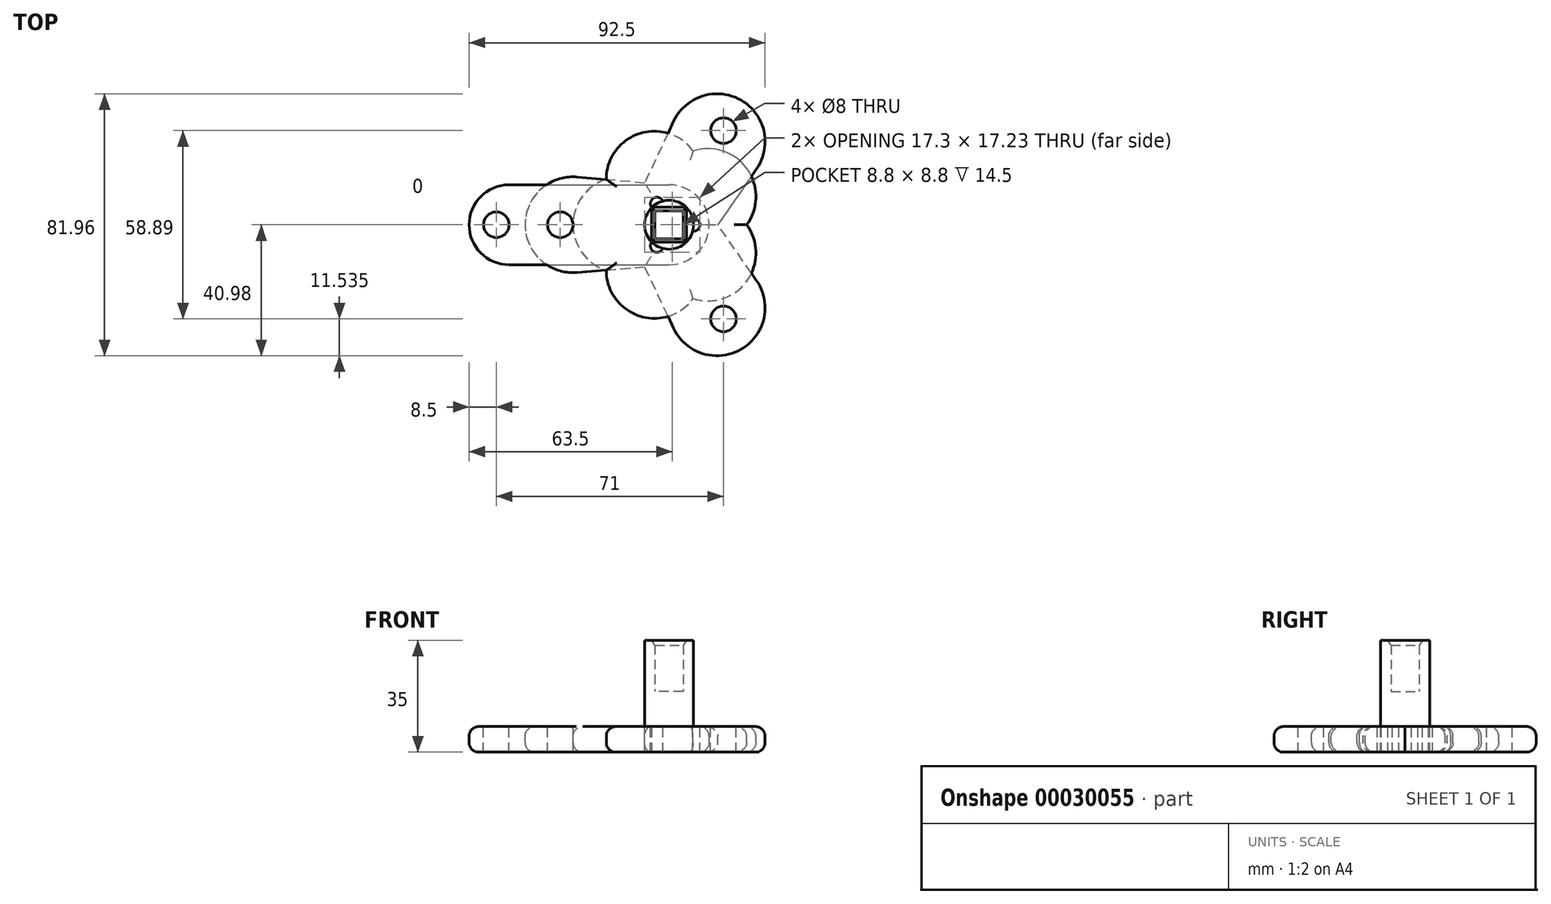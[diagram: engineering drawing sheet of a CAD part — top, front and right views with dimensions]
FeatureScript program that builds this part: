
annotation { "Feature Type Name" : "Feature", "Feature Type Description" : "" }
export const myFeature = defineFeature(function(context is Context, id is Id, definition is map)
    precondition{}
    {
        {
            var Q0;
            Q0=qCreatedBy(makeId("Top.planeOp"),FACE);
            var sketch = newSketch(context, id + "F0", { "sketchPlane" : qUnion([Q0])});
            skLineSegment(sketch, "E0.rect.bottom", {"start": v(4.4, -4.4) * mm, "end": v(-4.4, -4.4) * mm});
            skLineSegment(sketch, "E0.rect.top", {"start": v(4.4, 4.4) * mm, "end": v(-4.4, 4.4) * mm});
            skLineSegment(sketch, "E0.rect.left", {"start": v(4.4, -4.4) * mm, "end": v(4.4, 4.4) * mm});
            skLineSegment(sketch, "E0.rect.right", {"start": v(-4.4, -4.4) * mm, "end": v(-4.4, 4.4) * mm});
            skPoint(sketch, "E0.rect.middle", {"position": v(0, 0) * mm});
            skCircle(sketch, "E1", {"center": v(0, 0) * mm, "radius": 7.65 * mm});
            skArc(sketch, "E2", {"start": v(7.39, -1.98) * mm, "mid": v(9.65, 0) * mm, "end": v(7.39, 1.98) * mm});
            skArc(sketch, "E3.1.0", {"start": v(-1.98, 7.4) * mm, "mid": v(-4.82, 8.36) * mm, "end": v(-5.41, 5.4) * mm});
            skArc(sketch, "E3.2.0", {"start": v(-5.41, -5.4) * mm, "mid": v(-4.82, -8.36) * mm, "end": v(-1.98, -7.4) * mm});
            skSolve(sketch);
        }
        {
            var Q0;
            Q0=makeQuery(id+"F0.imprint","IMPRINT",FACE,{"disambiguationData":[TD([[makeQuery(id+"F0.imprint","IMPRINT",EDGE,{"derivedFrom":sQuery(id+"F0.wireOp",EDGE,"E0.rect.bottom")}),1.0]])]});
            extrude(context, id + "F1", {"entities" : qUnion([Q0]), "depth" : 27 * mm});
        }
        {
            var Q0;
            Q0=makeQuery(id+"F0.imprint","IMPRINT",FACE,{"disambiguationData":[TD([[makeQuery(id+"F0.imprint","IMPRINT",EDGE,{"derivedFrom":sQuery(id+"F0.wireOp",EDGE,"E0.rect.bottom")}),-1.0]])]});
            extrude(context, id + "F2", {"entities" : qUnion([Q0]), "operationType" : NewBodyOperationType.ADD, "depth" : 11 * mm});
        }
        {
            var Q0;
            Q0=makeQuery(id+"F1.opExtrude","CAP_EDGE",EDGE,{"disambiguationData":[OSD([sQuery(id+"F0.wireOp",EDGE,"E0.rect.top")])],"isStart":false});
            var Q1;
            Q1=makeQuery(id+"F1.opExtrude","CAP_EDGE",EDGE,{"disambiguationData":[OSD([sQuery(id+"F0.wireOp",EDGE,"E0.rect.right")])],"isStart":false});
            var Q2;
            Q2=makeQuery(id+"F1.opExtrude","CAP_EDGE",EDGE,{"disambiguationData":[OSD([sQuery(id+"F0.wireOp",EDGE,"E0.rect.bottom")])],"isStart":false});
            var Q3;
            Q3=makeQuery(id+"F1.opExtrude","CAP_EDGE",EDGE,{"disambiguationData":[OSD([sQuery(id+"F0.wireOp",EDGE,"E0.rect.left")])],"isStart":false});
            chamfer(context, id + "F3", {"entities" : qUnion([Q0, Q1, Q2, Q3]), "chamferType" : ChamferType.OFFSET_ANGLE, "width" : 1.5 * mm, "oppositeDirection" : false, "angle" : 35 * degree, "tangentPropagation" : true});
        }
        {
            var Q0;
            {var subQ0=sQuery(id+"F0.wireOp",EDGE,"E3.1.0");Q0=makeQuery(id+"F0.imprint","IMPRINT",FACE,{"disambiguationData":[TD([[makeQuery(id+"F0.imprint","IMPRINT",EDGE,{"derivedFrom":subQ0}),1.0]])]});}
            var Q1;
            {var subQ0=sQuery(id+"F0.wireOp",EDGE,"E3.2.0");Q1=makeQuery(id+"F0.imprint","IMPRINT",FACE,{"disambiguationData":[TD([[makeQuery(id+"F0.imprint","IMPRINT",EDGE,{"derivedFrom":subQ0}),1.0]])]});}
            var Q2;
            {var subQ0=sQuery(id+"F0.wireOp",EDGE,"E2");Q2=makeQuery(id+"F0.imprint","IMPRINT",FACE,{"disambiguationData":[TD([[makeQuery(id+"F0.imprint","IMPRINT",EDGE,{"derivedFrom":subQ0}),1.0]])]});}
            var Q3;
            Q3=makeQuery(id+"F0.imprint","IMPRINT",FACE,{"disambiguationData":[TD([[makeQuery(id+"F0.imprint","IMPRINT",EDGE,{"derivedFrom":sQuery(id+"F0.wireOp",EDGE,"E0.rect.bottom")}),1.0]])]});
            var Q4;
            Q4=makeQuery(id+"F0.imprint","IMPRINT",FACE,{"disambiguationData":[TD([[makeQuery(id+"F0.imprint","IMPRINT",EDGE,{"derivedFrom":sQuery(id+"F0.wireOp",EDGE,"E0.rect.bottom")}),-1.0]])]});
            extrude(context, id + "F4", {"entities" : qUnion([Q0, Q1, Q2, Q3, Q4]), "oppositeDirection" : true, "depth" : 8 * mm});
        }
        {
            var Q0;
            Q0=qCreatedBy(makeId("Top.planeOp"),FACE);
            var sketch = newSketch(context, id + "F5", { "sketchPlane" : qUnion([Q0])});
            skPoint(sketch, "E4.rect.middle", {"position": v(0, 0) * mm});
            skCircle(sketch, "E5", {"center": v(0, 0) * mm, "radius": 12.5 * mm});
            skCircle(sketch, "E6", {"center": v(-50, 0) * mm, "radius": 12.5 * mm});
            skLineSegment(sketch, "E7", {"start": v(-50, 12.5) * mm, "end": v(0, 12.5) * mm});
            skLineSegment(sketch, "E8", {"start": v(-50, -12.5) * mm, "end": v(0, -12.5) * mm});
            skLineSegment(sketch, "E9", {"start": v(-50, 0) * mm, "end": v(0, 0) * mm, "construction": true});
            skCircle(sketch, "E10", {"center": v(-54, 0) * mm, "radius": 4 * mm});
            skSolve(sketch);
        }
        {
            var Q0;
            Q0=makeQuery(id+"F5.imprint","IMPRINT",FACE,{"disambiguationData":[TD([[makeQuery(id+"F5.imprint","IMPRINT",EDGE,{"derivedFrom":sQuery(id+"F5.wireOp",EDGE,"E10")}),-1.0]])]});
            var Q1;
            {var subQ1=sQuery(id+"F5.wireOp",EDGE,"E7");Q1=makeQuery(id+"F5.imprint","IMPRINT",FACE,{"disambiguationData":[TD([[makeQuery(id+"F5.imprint","IMPRINT",EDGE,{"derivedFrom":subQ1}),-1.0]])]});}
            var Q2;
            {var subQ0=sQuery(id+"F5.wireOp",EDGE,"E5");var subQ2=makeQuery(id+"F5.imprint","INTERSECT",VERTEX,{"derivedFrom":[subQ0,sQuery(id+"F5.wireOp",EDGE,"E7")]});Q2=makeQuery(id+"F5.imprint","IMPRINT",FACE,{"disambiguationData":[TD([[makeQuery(id+"F5.imprint","IMPRINT",EDGE,{"disambiguationData":[TD([[subQ2,-1.0]])],"derivedFrom":subQ0}),1.0]])]});}
            extrude(context, id + "F6", {"entities" : qUnion([Q0, Q1, Q2]), "oppositeDirection" : true, "depth" : 8 * mm});
        }
        {
            var Q0;
            Q0=makeQuery(id+"F0.imprint","IMPRINT",FACE,{"disambiguationData":[TD([[makeQuery(id+"F0.imprint","IMPRINT",EDGE,{"derivedFrom":sQuery(id+"F0.wireOp",EDGE,"E0.rect.bottom")}),1.0]])]});
            var Q1;
            Q1=makeQuery(id+"F0.imprint","IMPRINT",FACE,{"disambiguationData":[TD([[makeQuery(id+"F0.imprint","IMPRINT",EDGE,{"derivedFrom":sQuery(id+"F0.wireOp",EDGE,"E0.rect.bottom")}),-1.0]])]});
            var Q2;
            {var subQ0=sQuery(id+"F0.wireOp",EDGE,"E3.2.0");Q2=makeQuery(id+"F0.imprint","IMPRINT",FACE,{"disambiguationData":[TD([[makeQuery(id+"F0.imprint","IMPRINT",EDGE,{"derivedFrom":subQ0}),1.0]])]});}
            var Q3;
            {var subQ0=sQuery(id+"F0.wireOp",EDGE,"E2");Q3=makeQuery(id+"F0.imprint","IMPRINT",FACE,{"disambiguationData":[TD([[makeQuery(id+"F0.imprint","IMPRINT",EDGE,{"derivedFrom":subQ0}),1.0]])]});}
            var Q4;
            {var subQ0=sQuery(id+"F0.wireOp",EDGE,"E3.1.0");Q4=makeQuery(id+"F0.imprint","IMPRINT",FACE,{"disambiguationData":[TD([[makeQuery(id+"F0.imprint","IMPRINT",EDGE,{"derivedFrom":subQ0}),1.0]])]});}
            var Q5;
            Q5=makeQuery(id+"F6.opExtrude","SWEPT_BODY",BODY,{"disambiguationData":[OSD([sQuery(id+"F5.wireOp",EDGE,"E5"),sQuery(id+"F5.wireOp",EDGE,"E6"),sQuery(id+"F5.wireOp",EDGE,"E7"),sQuery(id+"F5.wireOp",EDGE,"E8"),sQuery(id+"F5.wireOp",EDGE,"E10")])]});
            extrude(context, id + "F7", {"entities" : qUnion([Q0, Q1, Q2, Q3, Q4]), "operationType" : NewBodyOperationType.REMOVE, "endBound" : BoundingType.UP_TO_BODY, "oppositeDirection" : true, "endBoundEntityBody" : qUnion([Q5]), "depth" : 5 * mm});
        }
        {
            var Q0;
            Q0=makeQuery(id+"F6.opExtrude","CAP_EDGE",EDGE,{"disambiguationData":[OSD([sQuery(id+"F5.wireOp",EDGE,"E8")])],"isStart":true});
            var Q1;
            Q1=makeQuery(id+"F6.opExtrude","CAP_EDGE",EDGE,{"disambiguationData":[OSD([sQuery(id+"F5.wireOp",EDGE,"E8")])],"isStart":false});
            fillet(context, id + "F8", {"entities" : qUnion([Q0, Q1]), "radius" : 3 * mm, "tangentPropagation" : true, "allowEdgeOverflow" : false});
        }
        {
            var Q0;
            Q0=qCreatedBy(makeId("Top.planeOp"),FACE);
            var sketch = newSketch(context, id + "F9", { "sketchPlane" : qUnion([Q0])});
            skCircle(sketch, "E11", {"center": v(0, 0) * mm, "radius": 15 * mm});
            skCircle(sketch, "E12", {"center": v(-15, 0) * mm, "radius": 15 * mm});
            skCircle(sketch, "E13.1.0", {"center": v(-4.64, -14.27) * mm, "radius": 15 * mm});
            skCircle(sketch, "E13.2.0", {"center": v(12.14, -8.82) * mm, "radius": 15 * mm});
            skCircle(sketch, "E14.1.3.0", {"center": v(12.14, 8.82) * mm, "radius": 15 * mm});
            skCircle(sketch, "E14.1.4.0", {"center": v(-4.64, 14.27) * mm, "radius": 15 * mm});
            skSolve(sketch);
        }
        {
            var Q0;
            {var subQ0=sQuery(id+"F9.wireOp",EDGE,"E14.1.4.0");var subQ1=sQuery(id+"F9.wireOp",EDGE,"E11");var subQ2=makeQuery(id+"F9.imprint","INTERSECT",VERTEX,{"disambiguationData":[OD(0.0)],"derivedFrom":[subQ1,subQ0]});Q0=makeQuery(id+"F9.imprint","IMPRINT",FACE,{"disambiguationData":[TD([[makeQuery(id+"F9.imprint","IMPRINT",EDGE,{"disambiguationData":[TD([[subQ2,1.0]])],"derivedFrom":subQ1}),-1.0]])]});}
            var Q1;
            {var subQ1=sQuery(id+"F9.wireOp",EDGE,"E14.1.3.0");var subQ5=sQuery(id+"F9.wireOp",EDGE,"E11");var subQ6=makeQuery(id+"F9.imprint","INTERSECT",VERTEX,{"disambiguationData":[OD(0.0)],"derivedFrom":[subQ5,subQ1]});Q1=makeQuery(id+"F9.imprint","IMPRINT",FACE,{"disambiguationData":[TD([[makeQuery(id+"F9.imprint","IMPRINT",EDGE,{"disambiguationData":[TD([[subQ6,-1.0]])],"derivedFrom":subQ5}),-1.0]])]});}
            var Q2;
            {var subQ1=sQuery(id+"F9.wireOp",EDGE,"E11");var subQ3=sQuery(id+"F9.wireOp",EDGE,"E12");var subQ5=makeQuery(id+"F9.imprint","INTERSECT",VERTEX,{"disambiguationData":[OD(0.0)],"derivedFrom":[subQ1,subQ3]});Q2=makeQuery(id+"F9.imprint","IMPRINT",FACE,{"disambiguationData":[TD([[makeQuery(id+"F9.imprint","IMPRINT",EDGE,{"disambiguationData":[TD([[subQ5,-1.0]])],"derivedFrom":subQ1}),-1.0]])]});}
            var Q3;
            {var subQ0=sQuery(id+"F9.wireOp",EDGE,"E14.1.4.0");var subQ1=sQuery(id+"F9.wireOp",EDGE,"E11");var subQ2=makeQuery(id+"F9.imprint","INTERSECT",VERTEX,{"disambiguationData":[OD(1.0)],"derivedFrom":[subQ1,subQ0]});Q3=makeQuery(id+"F9.imprint","IMPRINT",FACE,{"disambiguationData":[TD([[makeQuery(id+"F9.imprint","IMPRINT",EDGE,{"disambiguationData":[TD([[subQ2,-1.0]])],"derivedFrom":subQ1}),-1.0]])]});}
            var Q4;
            {var subQ1=sQuery(id+"F9.wireOp",EDGE,"E11");var subQ5=sQuery(id+"F9.wireOp",EDGE,"E12");var subQ7=makeQuery(id+"F9.imprint","INTERSECT",VERTEX,{"disambiguationData":[OD(1.0)],"derivedFrom":[subQ1,subQ5]});Q4=makeQuery(id+"F9.imprint","IMPRINT",FACE,{"disambiguationData":[TD([[makeQuery(id+"F9.imprint","IMPRINT",EDGE,{"disambiguationData":[TD([[subQ7,-1.0]])],"derivedFrom":subQ1}),-1.0]])]});}
            var Q5;
            {var subQ0=sQuery(id+"F9.wireOp",EDGE,"E13.2.0");var subQ1=sQuery(id+"F9.wireOp",EDGE,"E11");var subQ2=makeQuery(id+"F9.imprint","INTERSECT",VERTEX,{"disambiguationData":[OD(1.0)],"derivedFrom":[subQ1,subQ0]});Q5=makeQuery(id+"F9.imprint","IMPRINT",FACE,{"disambiguationData":[TD([[makeQuery(id+"F9.imprint","IMPRINT",EDGE,{"disambiguationData":[TD([[subQ2,-1.0]])],"derivedFrom":subQ1}),-1.0]])]});}
            var Q6;
            {var subQ1=sQuery(id+"F9.wireOp",EDGE,"E11");var subQ5=sQuery(id+"F9.wireOp",EDGE,"E13.1.0");var subQ7=makeQuery(id+"F9.imprint","INTERSECT",VERTEX,{"disambiguationData":[OD(1.0)],"derivedFrom":[subQ1,subQ5]});Q6=makeQuery(id+"F9.imprint","IMPRINT",FACE,{"disambiguationData":[TD([[makeQuery(id+"F9.imprint","IMPRINT",EDGE,{"disambiguationData":[TD([[subQ7,-1.0]])],"derivedFrom":subQ1}),-1.0]])]});}
            var Q7;
            {var subQ1=sQuery(id+"F9.wireOp",EDGE,"E11");var subQ3=sQuery(id+"F9.wireOp",EDGE,"E13.2.0");var subQ5=makeQuery(id+"F9.imprint","INTERSECT",VERTEX,{"disambiguationData":[OD(0.0)],"derivedFrom":[subQ1,subQ3]});Q7=makeQuery(id+"F9.imprint","IMPRINT",FACE,{"disambiguationData":[TD([[makeQuery(id+"F9.imprint","IMPRINT",EDGE,{"disambiguationData":[TD([[subQ5,1.0]])],"derivedFrom":subQ1}),-1.0]])]});}
            var Q8;
            {var subQ0=sQuery(id+"F9.wireOp",EDGE,"E14.1.4.0");var subQ3=sQuery(id+"F9.wireOp",EDGE,"E11");var subQ4=makeQuery(id+"F9.imprint","INTERSECT",VERTEX,{"disambiguationData":[OD(0.0)],"derivedFrom":[subQ3,subQ0]});Q8=makeQuery(id+"F9.imprint","IMPRINT",FACE,{"disambiguationData":[TD([[makeQuery(id+"F9.imprint","IMPRINT",EDGE,{"disambiguationData":[TD([[subQ4,-1.0]])],"derivedFrom":subQ3}),1.0]])]});}
            var Q9;
            {var subQ0=sQuery(id+"F9.wireOp",EDGE,"E13.2.0");var subQ1=sQuery(id+"F9.wireOp",EDGE,"E12");var subQ3=makeQuery(id+"F9.imprint","INTERSECT",VERTEX,{"derivedFrom":[subQ1,subQ0]});Q9=makeQuery(id+"F9.imprint","IMPRINT",FACE,{"disambiguationData":[TD([[makeQuery(id+"F9.imprint","IMPRINT",EDGE,{"disambiguationData":[TD([[subQ3,-1.0]])],"derivedFrom":subQ1}),1.0]])]});}
            var Q10;
            {var subQ1=sQuery(id+"F9.wireOp",EDGE,"E13.1.0");var subQ3=sQuery(id+"F9.wireOp",EDGE,"E11");var subQ5=makeQuery(id+"F9.imprint","INTERSECT",VERTEX,{"disambiguationData":[OD(1.0)],"derivedFrom":[subQ3,subQ1]});Q10=makeQuery(id+"F9.imprint","IMPRINT",FACE,{"disambiguationData":[TD([[makeQuery(id+"F9.imprint","IMPRINT",EDGE,{"disambiguationData":[TD([[subQ5,-1.0]])],"derivedFrom":subQ3}),1.0]])]});}
            var Q11;
            {var subQ3=sQuery(id+"F9.wireOp",EDGE,"E11");var subQ6=sQuery(id+"F9.wireOp",EDGE,"E12");var subQ9=makeQuery(id+"F9.imprint","INTERSECT",VERTEX,{"disambiguationData":[OD(0.0)],"derivedFrom":[subQ3,subQ6]});Q11=makeQuery(id+"F9.imprint","IMPRINT",FACE,{"disambiguationData":[TD([[makeQuery(id+"F9.imprint","IMPRINT",EDGE,{"disambiguationData":[TD([[subQ9,-1.0]])],"derivedFrom":subQ3}),1.0]])]});}
            var Q12;
            {var subQ0=sQuery(id+"F9.wireOp",EDGE,"E14.1.4.0");var subQ1=sQuery(id+"F9.wireOp",EDGE,"E13.1.0");var subQ3=makeQuery(id+"F9.imprint","INTERSECT",VERTEX,{"derivedFrom":[subQ1,subQ0]});Q12=makeQuery(id+"F9.imprint","IMPRINT",FACE,{"disambiguationData":[TD([[makeQuery(id+"F9.imprint","IMPRINT",EDGE,{"disambiguationData":[TD([[subQ3,1.0]])],"derivedFrom":subQ1}),1.0]])]});}
            var Q13;
            {var subQ0=sQuery(id+"F9.wireOp",EDGE,"E14.1.3.0");var subQ1=sQuery(id+"F9.wireOp",EDGE,"E13.1.0");var subQ3=makeQuery(id+"F9.imprint","INTERSECT",VERTEX,{"derivedFrom":[subQ1,subQ0]});Q13=makeQuery(id+"F9.imprint","IMPRINT",FACE,{"disambiguationData":[TD([[makeQuery(id+"F9.imprint","IMPRINT",EDGE,{"disambiguationData":[TD([[subQ3,-1.0]])],"derivedFrom":subQ1}),1.0]])]});}
            var Q14;
            {var subQ0=sQuery(id+"F9.wireOp",EDGE,"E14.1.4.0");var subQ1=sQuery(id+"F9.wireOp",EDGE,"E13.2.0");var subQ3=makeQuery(id+"F9.imprint","INTERSECT",VERTEX,{"derivedFrom":[subQ1,subQ0]});Q14=makeQuery(id+"F9.imprint","IMPRINT",FACE,{"disambiguationData":[TD([[makeQuery(id+"F9.imprint","IMPRINT",EDGE,{"disambiguationData":[TD([[subQ3,-1.0]])],"derivedFrom":subQ1}),1.0]])]});}
            var Q15;
            {var subQ0=sQuery(id+"F9.wireOp",EDGE,"E14.1.4.0");var subQ3=sQuery(id+"F9.wireOp",EDGE,"E11");var subQ4=makeQuery(id+"F9.imprint","INTERSECT",VERTEX,{"disambiguationData":[OD(0.0)],"derivedFrom":[subQ3,subQ0]});Q15=makeQuery(id+"F9.imprint","IMPRINT",FACE,{"disambiguationData":[TD([[makeQuery(id+"F9.imprint","IMPRINT",EDGE,{"disambiguationData":[TD([[subQ4,1.0]])],"derivedFrom":subQ3}),1.0]])]});}
            var Q16;
            {var subQ0=sQuery(id+"F9.wireOp",EDGE,"E14.1.4.0");var subQ1=sQuery(id+"F9.wireOp",EDGE,"E11");var subQ2=makeQuery(id+"F9.imprint","INTERSECT",VERTEX,{"disambiguationData":[OD(0.0)],"derivedFrom":[subQ1,subQ0]});Q16=makeQuery(id+"F9.imprint","IMPRINT",FACE,{"disambiguationData":[TD([[makeQuery(id+"F9.imprint","IMPRINT",EDGE,{"disambiguationData":[TD([[subQ2,-1.0]])],"derivedFrom":subQ1}),-1.0]])]});}
            var Q17;
            {var subQ0=sQuery(id+"F9.wireOp",EDGE,"E14.1.3.0");var subQ3=sQuery(id+"F9.wireOp",EDGE,"E11");var subQ4=makeQuery(id+"F9.imprint","INTERSECT",VERTEX,{"disambiguationData":[OD(0.0)],"derivedFrom":[subQ3,subQ0]});Q17=makeQuery(id+"F9.imprint","IMPRINT",FACE,{"disambiguationData":[TD([[makeQuery(id+"F9.imprint","IMPRINT",EDGE,{"disambiguationData":[TD([[subQ4,-1.0]])],"derivedFrom":subQ3}),1.0]])]});}
            var Q18;
            {var subQ2=sQuery(id+"F9.wireOp",EDGE,"E13.2.0");var subQ7=sQuery(id+"F9.wireOp",EDGE,"E11");var subQ9=makeQuery(id+"F9.imprint","INTERSECT",VERTEX,{"disambiguationData":[OD(0.0)],"derivedFrom":[subQ7,subQ2]});Q18=makeQuery(id+"F9.imprint","IMPRINT",FACE,{"disambiguationData":[TD([[makeQuery(id+"F9.imprint","IMPRINT",EDGE,{"disambiguationData":[TD([[subQ9,1.0]])],"derivedFrom":subQ7}),1.0]])]});}
            var Q19;
            {var subQ0=sQuery(id+"F9.wireOp",EDGE,"E14.1.4.0");var subQ3=sQuery(id+"F9.wireOp",EDGE,"E11");var subQ4=makeQuery(id+"F9.imprint","INTERSECT",VERTEX,{"disambiguationData":[OD(1.0)],"derivedFrom":[subQ3,subQ0]});Q19=makeQuery(id+"F9.imprint","IMPRINT",FACE,{"disambiguationData":[TD([[makeQuery(id+"F9.imprint","IMPRINT",EDGE,{"disambiguationData":[TD([[subQ4,-1.0]])],"derivedFrom":subQ3}),1.0]])]});}
            var Q20;
            {var subQ3=sQuery(id+"F9.wireOp",EDGE,"E13.2.0");var subQ7=sQuery(id+"F9.wireOp",EDGE,"E11");var subQ8=makeQuery(id+"F9.imprint","INTERSECT",VERTEX,{"disambiguationData":[OD(1.0)],"derivedFrom":[subQ7,subQ3]});Q20=makeQuery(id+"F9.imprint","IMPRINT",FACE,{"disambiguationData":[TD([[makeQuery(id+"F9.imprint","IMPRINT",EDGE,{"disambiguationData":[TD([[subQ8,-1.0]])],"derivedFrom":subQ7}),1.0]])]});}
            var Q21;
            {var subQ0=sQuery(id+"F9.wireOp",EDGE,"E13.1.0");var subQ1=sQuery(id+"F9.wireOp",EDGE,"E11");var subQ2=makeQuery(id+"F9.imprint","INTERSECT",VERTEX,{"disambiguationData":[OD(0.0)],"derivedFrom":[subQ1,subQ0]});Q21=makeQuery(id+"F9.imprint","IMPRINT",FACE,{"disambiguationData":[TD([[makeQuery(id+"F9.imprint","IMPRINT",EDGE,{"disambiguationData":[TD([[subQ2,-1.0]])],"derivedFrom":subQ1}),-1.0]])]});}
            var Q22;
            {var subQ0=sQuery(id+"F9.wireOp",EDGE,"E14.1.3.0");var subQ1=sQuery(id+"F9.wireOp",EDGE,"E12");var subQ3=makeQuery(id+"F9.imprint","INTERSECT",VERTEX,{"derivedFrom":[subQ1,subQ0]});Q22=makeQuery(id+"F9.imprint","IMPRINT",FACE,{"disambiguationData":[TD([[makeQuery(id+"F9.imprint","IMPRINT",EDGE,{"disambiguationData":[TD([[subQ3,1.0]])],"derivedFrom":subQ1}),1.0]])]});}
            var Q23;
            {var subQ1=sQuery(id+"F9.wireOp",EDGE,"E12");var subQ3=sQuery(id+"F9.wireOp",EDGE,"E11");var subQ5=makeQuery(id+"F9.imprint","INTERSECT",VERTEX,{"disambiguationData":[OD(1.0)],"derivedFrom":[subQ3,subQ1]});Q23=makeQuery(id+"F9.imprint","IMPRINT",FACE,{"disambiguationData":[TD([[makeQuery(id+"F9.imprint","IMPRINT",EDGE,{"disambiguationData":[TD([[subQ5,-1.0]])],"derivedFrom":subQ3}),1.0]])]});}
            var Q24;
            {var subQ2=sQuery(id+"F9.wireOp",EDGE,"E13.1.0");var subQ7=sQuery(id+"F9.wireOp",EDGE,"E11");var subQ8=makeQuery(id+"F9.imprint","INTERSECT",VERTEX,{"disambiguationData":[OD(0.0)],"derivedFrom":[subQ7,subQ2]});Q24=makeQuery(id+"F9.imprint","IMPRINT",FACE,{"disambiguationData":[TD([[makeQuery(id+"F9.imprint","IMPRINT",EDGE,{"disambiguationData":[TD([[subQ8,-1.0]])],"derivedFrom":subQ7}),1.0]])]});}
            extrude(context, id + "F10", {"entities" : qUnion([Q0, Q1, Q2, Q3, Q4, Q5, Q6, Q7, Q8, Q9, Q10, Q11, Q12, Q13, Q14, Q15, Q16, Q17, Q18, Q19, Q20, Q21, Q22, Q23, Q24]), "oppositeDirection" : true, "depth" : 8 * mm});
        }
        {
            var Q0;
            Q0=makeQuery(id+"F0.imprint","IMPRINT",FACE,{"disambiguationData":[TD([[makeQuery(id+"F0.imprint","IMPRINT",EDGE,{"derivedFrom":sQuery(id+"F0.wireOp",EDGE,"E0.rect.bottom")}),-1.0]])]});
            var Q1;
            {var subQ0=sQuery(id+"F0.wireOp",EDGE,"E3.1.0");Q1=makeQuery(id+"F0.imprint","IMPRINT",FACE,{"disambiguationData":[TD([[makeQuery(id+"F0.imprint","IMPRINT",EDGE,{"derivedFrom":subQ0}),1.0]])]});}
            var Q2;
            {var subQ0=sQuery(id+"F0.wireOp",EDGE,"E3.2.0");Q2=makeQuery(id+"F0.imprint","IMPRINT",FACE,{"disambiguationData":[TD([[makeQuery(id+"F0.imprint","IMPRINT",EDGE,{"derivedFrom":subQ0}),1.0]])]});}
            var Q3;
            {var subQ0=sQuery(id+"F0.wireOp",EDGE,"E2");Q3=makeQuery(id+"F0.imprint","IMPRINT",FACE,{"disambiguationData":[TD([[makeQuery(id+"F0.imprint","IMPRINT",EDGE,{"derivedFrom":subQ0}),1.0]])]});}
            var Q4;
            Q4=makeQuery(id+"F0.imprint","IMPRINT",FACE,{"disambiguationData":[TD([[makeQuery(id+"F0.imprint","IMPRINT",EDGE,{"derivedFrom":sQuery(id+"F0.wireOp",EDGE,"E0.rect.bottom")}),1.0]])]});
            var Q5;
            Q5=makeQuery(id+"F10.opExtrude","SWEPT_BODY",BODY,{"disambiguationData":[OSD([sQuery(id+"F9.wireOp",EDGE,"E12"),sQuery(id+"F9.wireOp",EDGE,"E13.1.0"),sQuery(id+"F9.wireOp",EDGE,"E13.2.0"),sQuery(id+"F9.wireOp",EDGE,"E14.1.3.0"),sQuery(id+"F9.wireOp",EDGE,"E14.1.4.0")])]});
            extrude(context, id + "F11", {"entities" : qUnion([Q0, Q1, Q2, Q3, Q4]), "operationType" : NewBodyOperationType.REMOVE, "endBound" : BoundingType.UP_TO_BODY, "oppositeDirection" : true, "endBoundEntityBody" : qUnion([Q5]), "depth" : 25 * mm});
        }
        {
            var Q0;
            Q0=makeQuery(id+"F10.opExtrude","CAP_EDGE",EDGE,{"disambiguationData":[OSD([sQuery(id+"F9.wireOp",EDGE,"E14.1.3.0")])],"isStart":true});
            var Q1;
            Q1=makeQuery(id+"F10.opExtrude","CAP_EDGE",EDGE,{"disambiguationData":[OSD([sQuery(id+"F9.wireOp",EDGE,"E14.1.4.0")])],"isStart":true});
            var Q2;
            Q2=makeQuery(id+"F10.opExtrude","CAP_EDGE",EDGE,{"disambiguationData":[OSD([sQuery(id+"F9.wireOp",EDGE,"E12")])],"isStart":true});
            var Q3;
            Q3=makeQuery(id+"F10.opExtrude","CAP_EDGE",EDGE,{"disambiguationData":[OSD([sQuery(id+"F9.wireOp",EDGE,"E13.1.0")])],"isStart":true});
            var Q4;
            Q4=makeQuery(id+"F10.opExtrude","CAP_EDGE",EDGE,{"disambiguationData":[OSD([sQuery(id+"F9.wireOp",EDGE,"E13.2.0")])],"isStart":true});
            var Q5;
            Q5=makeQuery(id+"F10.opExtrude","CAP_EDGE",EDGE,{"disambiguationData":[OSD([sQuery(id+"F9.wireOp",EDGE,"E14.1.3.0")])],"isStart":false});
            var Q6;
            Q6=makeQuery(id+"F10.opExtrude","CAP_EDGE",EDGE,{"disambiguationData":[OSD([sQuery(id+"F9.wireOp",EDGE,"E14.1.4.0")])],"isStart":false});
            var Q7;
            Q7=makeQuery(id+"F10.opExtrude","CAP_EDGE",EDGE,{"disambiguationData":[OSD([sQuery(id+"F9.wireOp",EDGE,"E12")])],"isStart":false});
            var Q8;
            Q8=makeQuery(id+"F10.opExtrude","CAP_EDGE",EDGE,{"disambiguationData":[OSD([sQuery(id+"F9.wireOp",EDGE,"E13.1.0")])],"isStart":false});
            var Q9;
            Q9=makeQuery(id+"F10.opExtrude","CAP_EDGE",EDGE,{"disambiguationData":[OSD([sQuery(id+"F9.wireOp",EDGE,"E13.2.0")])],"isStart":false});
            fillet(context, id + "F12", {"entities" : qUnion([Q0, Q1, Q2, Q3, Q4, Q5, Q6, Q7, Q8, Q9]), "radius" : 3 * mm, "tangentPropagation" : true, "allowEdgeOverflow" : false});
        }
        {
            var Q0;
            Q0=qCreatedBy(makeId("Top.planeOp"),FACE);
            var sketch = newSketch(context, id + "F13", { "sketchPlane" : qUnion([Q0])});
            skPoint(sketch, "E15.rect.middle", {"position": v(0, 0) * mm});
            skCircle(sketch, "E16", {"center": v(0, 0) * mm, "radius": 12.5 * mm});
            skCircle(sketch, "E17", {"center": v(-30, 0) * mm, "radius": 15 * mm});
            skLineSegment(sketch, "E18", {"start": v(-28.75, 14.95) * mm, "end": v(1.04, 12.46) * mm});
            skLineSegment(sketch, "E19", {"start": v(-28.75, -14.95) * mm, "end": v(1.04, -12.46) * mm});
            skLineSegment(sketch, "E20", {"start": v(-30, 0) * mm, "end": v(0, 0) * mm, "construction": true});
            skCircle(sketch, "E21", {"center": v(-34, 0) * mm, "radius": 4 * mm});
            skCircle(sketch, "E22.1.0", {"center": v(17, -29.44) * mm, "radius": 4 * mm});
            skCircle(sketch, "E22.1.1", {"center": v(15, -25.98) * mm, "radius": 15 * mm});
            skLineSegment(sketch, "E22.1.2", {"start": v(1.43, -32.37) * mm, "end": v(-11.3, -5.33) * mm});
            skLineSegment(sketch, "E22.1.3", {"start": v(27.32, -17.42) * mm, "end": v(10.27, 7.13) * mm});
            skCircle(sketch, "E22.2.0", {"center": v(17, 29.44) * mm, "radius": 4 * mm});
            skCircle(sketch, "E22.2.1", {"center": v(15, 25.98) * mm, "radius": 15 * mm});
            skLineSegment(sketch, "E22.2.2", {"start": v(27.32, 17.42) * mm, "end": v(10.27, -7.13) * mm});
            skLineSegment(sketch, "E22.2.3", {"start": v(1.43, 32.37) * mm, "end": v(-11.3, 5.33) * mm});
            skSolve(sketch);
        }
        {
            var Q0;
            {var subQ3=sQuery(id+"F13.wireOp",EDGE,"E16");var subQ5=sQuery(id+"F13.wireOp",EDGE,"E22.1.2");var subQ8=makeQuery(id+"F13.imprint","INTERSECT",VERTEX,{"derivedFrom":[subQ3,subQ5]});Q0=makeQuery(id+"F13.imprint","IMPRINT",FACE,{"disambiguationData":[TD([[makeQuery(id+"F13.imprint","IMPRINT",EDGE,{"disambiguationData":[TD([[subQ8,1.0]])],"derivedFrom":subQ3}),-1.0]])]});}
            var Q1;
            {var subQ7=sQuery(id+"F13.wireOp",EDGE,"E16");var subQ9=sQuery(id+"F13.wireOp",EDGE,"E18");var subQ11=makeQuery(id+"F13.imprint","INTERSECT",VERTEX,{"derivedFrom":[subQ7,subQ9]});Q1=makeQuery(id+"F13.imprint","IMPRINT",FACE,{"disambiguationData":[TD([[makeQuery(id+"F13.imprint","IMPRINT",EDGE,{"disambiguationData":[TD([[subQ11,1.0]])],"derivedFrom":subQ7}),-1.0]])]});}
            var Q2;
            Q2=makeQuery(id+"F13.imprint","IMPRINT",FACE,{"disambiguationData":[TD([[makeQuery(id+"F13.imprint","IMPRINT",EDGE,{"derivedFrom":sQuery(id+"F13.wireOp",EDGE,"E22.1.0")}),-1.0]])]});
            var Q3;
            {var subQ1=sQuery(id+"F13.wireOp",EDGE,"E22.1.3");var subQ3=sQuery(id+"F13.wireOp",EDGE,"E16");var subQ5=makeQuery(id+"F13.imprint","INTERSECT",VERTEX,{"derivedFrom":[subQ3,subQ1]});Q3=makeQuery(id+"F13.imprint","IMPRINT",FACE,{"disambiguationData":[TD([[makeQuery(id+"F13.imprint","IMPRINT",EDGE,{"disambiguationData":[TD([[subQ5,1.0]])],"derivedFrom":subQ3}),-1.0]])]});}
            var Q4;
            {var subQ1=sQuery(id+"F13.wireOp",EDGE,"E19");var subQ3=sQuery(id+"F13.wireOp",EDGE,"E16");var subQ5=makeQuery(id+"F13.imprint","INTERSECT",VERTEX,{"derivedFrom":[subQ3,subQ1]});Q4=makeQuery(id+"F13.imprint","IMPRINT",FACE,{"disambiguationData":[TD([[makeQuery(id+"F13.imprint","IMPRINT",EDGE,{"disambiguationData":[TD([[subQ5,1.0]])],"derivedFrom":subQ3}),-1.0]])]});}
            var Q5;
            {var subQ0=sQuery(id+"F13.wireOp",EDGE,"E18");var subQ3=sQuery(id+"F13.wireOp",EDGE,"E16");var subQ4=makeQuery(id+"F13.imprint","INTERSECT",VERTEX,{"derivedFrom":[subQ3,subQ0]});Q5=makeQuery(id+"F13.imprint","IMPRINT",FACE,{"disambiguationData":[TD([[makeQuery(id+"F13.imprint","IMPRINT",EDGE,{"disambiguationData":[TD([[subQ4,-1.0]])],"derivedFrom":subQ3}),-1.0]])]});}
            var Q6;
            {var subQ3=sQuery(id+"F13.wireOp",EDGE,"E16");var subQ8=sQuery(id+"F13.wireOp",EDGE,"E19");var subQ11=makeQuery(id+"F13.imprint","INTERSECT",VERTEX,{"derivedFrom":[subQ3,subQ8]});Q6=makeQuery(id+"F13.imprint","IMPRINT",FACE,{"disambiguationData":[TD([[makeQuery(id+"F13.imprint","IMPRINT",EDGE,{"disambiguationData":[TD([[subQ11,-1.0]])],"derivedFrom":subQ3}),-1.0]])]});}
            var Q7;
            {var subQ0=sQuery(id+"F13.wireOp",EDGE,"E16");var subQ6=makeQuery(id+"F13.imprint","INTERSECT",VERTEX,{"derivedFrom":[subQ0,sQuery(id+"F13.wireOp",EDGE,"E18")]});Q7=makeQuery(id+"F13.imprint","IMPRINT",FACE,{"disambiguationData":[TD([[makeQuery(id+"F13.imprint","IMPRINT",EDGE,{"disambiguationData":[TD([[subQ6,1.0]])],"derivedFrom":subQ0}),1.0]])]});}
            var Q8;
            Q8=makeQuery(id+"F13.imprint","IMPRINT",FACE,{"disambiguationData":[TD([[makeQuery(id+"F13.imprint","IMPRINT",EDGE,{"derivedFrom":sQuery(id+"F13.wireOp",EDGE,"E22.2.0")}),-1.0]])]});
            var Q9;
            Q9=makeQuery(id+"F13.imprint","IMPRINT",FACE,{"disambiguationData":[TD([[makeQuery(id+"F13.imprint","IMPRINT",EDGE,{"derivedFrom":sQuery(id+"F13.wireOp",EDGE,"E21")}),-1.0]])]});
            extrude(context, id + "F14", {"entities" : qUnion([Q0, Q1, Q2, Q3, Q4, Q5, Q6, Q7, Q8, Q9]), "oppositeDirection" : true, "depth" : 8 * mm});
        }
        {
            var Q0;
            Q0=makeQuery(id+"F0.imprint","IMPRINT",FACE,{"disambiguationData":[TD([[makeQuery(id+"F0.imprint","IMPRINT",EDGE,{"derivedFrom":sQuery(id+"F0.wireOp",EDGE,"E0.rect.bottom")}),-1.0]])]});
            var Q1;
            {var subQ0=sQuery(id+"F0.wireOp",EDGE,"E3.2.0");Q1=makeQuery(id+"F0.imprint","IMPRINT",FACE,{"disambiguationData":[TD([[makeQuery(id+"F0.imprint","IMPRINT",EDGE,{"derivedFrom":subQ0}),1.0]])]});}
            var Q2;
            {var subQ0=sQuery(id+"F0.wireOp",EDGE,"E2");Q2=makeQuery(id+"F0.imprint","IMPRINT",FACE,{"disambiguationData":[TD([[makeQuery(id+"F0.imprint","IMPRINT",EDGE,{"derivedFrom":subQ0}),1.0]])]});}
            var Q3;
            Q3=makeQuery(id+"F0.imprint","IMPRINT",FACE,{"disambiguationData":[TD([[makeQuery(id+"F0.imprint","IMPRINT",EDGE,{"derivedFrom":sQuery(id+"F0.wireOp",EDGE,"E0.rect.bottom")}),1.0]])]});
            var Q4;
            {var subQ0=sQuery(id+"F0.wireOp",EDGE,"E3.1.0");Q4=makeQuery(id+"F0.imprint","IMPRINT",FACE,{"disambiguationData":[TD([[makeQuery(id+"F0.imprint","IMPRINT",EDGE,{"derivedFrom":subQ0}),1.0]])]});}
            extrude(context, id + "F15", {"entities" : qUnion([Q0, Q1, Q2, Q3, Q4]), "operationType" : NewBodyOperationType.REMOVE, "oppositeDirection" : true, "depth" : 8 * mm});
        }
        {
            var Q0;
            Q0=makeQuery(id+"F14.opExtrude","CAP_EDGE",EDGE,{"disambiguationData":[OSD([sQuery(id+"F13.wireOp",EDGE,"E22.1.1")])],"isStart":true});
            var Q1;
            Q1=makeQuery(id+"F14.opExtrude","CAP_EDGE",EDGE,{"disambiguationData":[OSD([sQuery(id+"F13.wireOp",EDGE,"E22.2.1")])],"isStart":true});
            var Q2;
            Q2=makeQuery(id+"F14.opExtrude","CAP_EDGE",EDGE,{"disambiguationData":[OSD([sQuery(id+"F13.wireOp",EDGE,"E17")])],"isStart":true});
            var Q3;
            Q3=makeQuery(id+"F14.opExtrude","CAP_EDGE",EDGE,{"disambiguationData":[OSD([sQuery(id+"F13.wireOp",EDGE,"E22.1.1")])],"isStart":false});
            var Q4;
            Q4=makeQuery(id+"F14.opExtrude","CAP_EDGE",EDGE,{"disambiguationData":[OSD([sQuery(id+"F13.wireOp",EDGE,"E22.2.1")])],"isStart":false});
            var Q5;
            Q5=makeQuery(id+"F14.opExtrude","CAP_EDGE",EDGE,{"disambiguationData":[OSD([sQuery(id+"F13.wireOp",EDGE,"E17")])],"isStart":false});
            fillet(context, id + "F16", {"entities" : qUnion([Q0, Q1, Q2, Q3, Q4, Q5]), "radius" : 3 * mm, "tangentPropagation" : true, "allowEdgeOverflow" : false});
        }
    });
